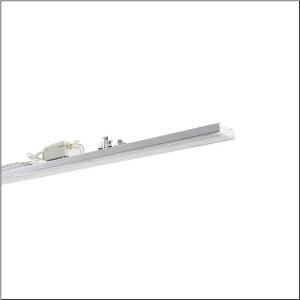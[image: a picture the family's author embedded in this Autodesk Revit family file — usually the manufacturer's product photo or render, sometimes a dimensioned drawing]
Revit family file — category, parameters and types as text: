
# Revit family: licross_11_recessed_mo_51te1edv4e5g
name_source: partatom
category: Lighting Fixtures
units: mm (PartAtom-declared; Revit-internal decimal feet)

## family parameters
Cut with Voids When Loaded = No
Host = Face
Light Source = No
Part Type = Normal
Room Calculation Point = No
Round Connector Dimension = Use Diameter
Shared = No

## types (1)
- --- (1 x LED, 14850 lm, 84.1 W, 4000K)
    Apparent Load = 84 VA
    CIE Flux Codes = 85 95 99 100 100
    Color Rendering = 80
    Color Temperature = 4000K
    Default Elevation = 1800 mm
    Description = Licross 11 Recessed MO, luminaire insert, of sheet steel, galvanised, coil coated, white, length: 2.250mm, width: 66mm, height: 67mm, LED rated luminous flux: 14.850lm, light colour: 840, SDCM (Standard Deviation of Colour Matching)MacAdam ≤ 2 SDCM (initial), control gear: DALI 2, with plug, 5-pole, with phase selection, mains connection: 220..240V, AC, 50/60Hz, rated input power: 84W, internal wiring halogen-free, primary light control with lens, of plastic, primary optical cover: cover, of PMMA, light emission: direct distribution, primary light characteristic: symmetric, protection rating (complete): IP54, insulation class (complete): insulation class I (protective earthing), certification: CE, ENEC, VDE, UKCA, protection symbol: D if used in an environment with non-conductive dust loads with corresponding accessories, impact resistance: IK06, permissible ambient temperature for indoor applications: -25..+35°C, corresponds to IFS (International Featured Standards) requirements for safety and quality in the food industry, reducing of maximum allowable ambient temperature of 5°C with ceiling mounting, LABS conformity tested according to VDMA 24364:2018-05, The light source and the operating device comply with the requirements of the Ecodesign Regulation (EU) 2019/2020 and are replaceable in accordance with this regulation, packaging unit: 1 piece
    Height = 58 mm
    Lamp = 1 x LED
    Lamp Light Flux = 14850 lm
    Lamp Power = 84.1 W
    Lamp count = 1
    Length = 2250 mm
    Luminous efficacy = 177 lm/W
    Manufacturer = Siteco
    ModVariant = No
    Model = 51TE1EDV4E5G
    Mounting Place = Ceiling
    Mounting Type = Pendant
    Number of Poles = 1
    OnlyDefault = Yes
    Power Factor = 1
    Product Name = Licross 11 Recessed MO
    Product group = luminaire insert | ceiling pendant
    ProductGroupID = 901
    Protection Class = Protection class I
    Protection Degree = IP 54
    RLX_Detail_Level = 1
    RLX_Emergency_Light_Flux = 0 lm
    RLX_Emergency_Type = 0
    RLX_Emergency_Type_DB = No
    RlxData = <blob elided: 29957 chars, md5=e5417459>
    Socket = socket
    Standby Power = 0 W
    System Light Flux = 14850 lm
    System Power = 84 W
    Type Comments = factory setting: luminous flux: 100 % | dim-lin: 254 | 378 mA
    Type Image = l_1296930.jpg
    URL = http://relux.com
    VarID = @adj_101201
    Voltage = 0 V
    Weight = 0.00 kg
    Width = 66 mm

## geometry (parser evidence)
native form markers: Blend x4, Sweep x9
no freeform markers — native parametric forms only
